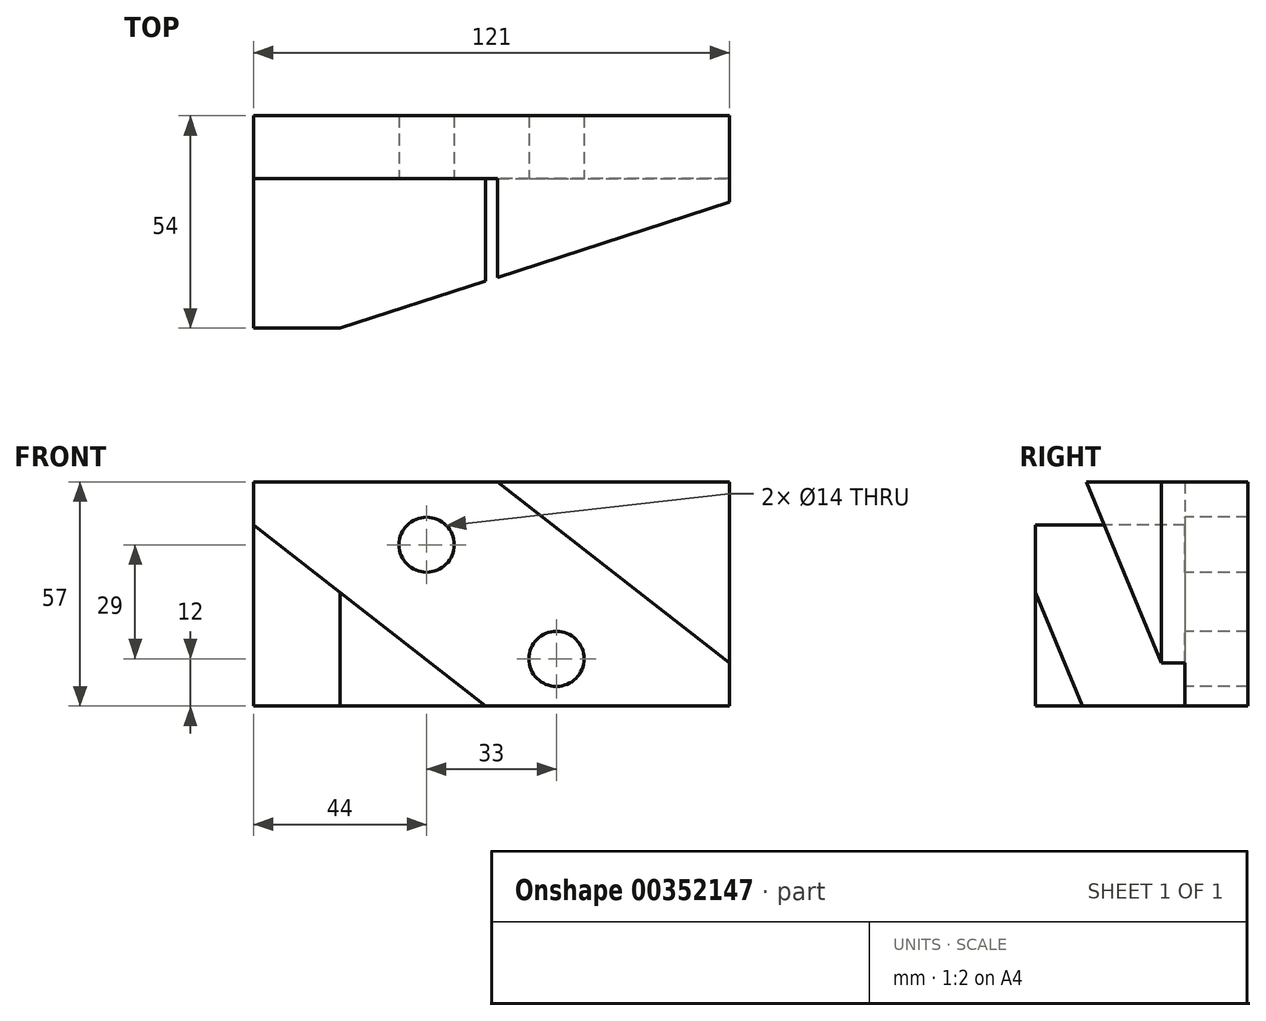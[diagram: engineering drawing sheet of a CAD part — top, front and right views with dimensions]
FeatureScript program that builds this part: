
annotation { "Feature Type Name" : "Feature", "Feature Type Description" : "" }
export const myFeature = defineFeature(function(context is Context, id is Id, definition is map)
    precondition{}
    {
        {
            var Q0;
            Q0=qCreatedBy(makeId("Front.planeOp"),FACE);
            var sketch = newSketch(context, id + "F0", { "sketchPlane" : qUnion([Q0])});
            skLineSegment(sketch, "E0", {"start": v(0, 0) * mm, "end": v(0, 46) * mm});
            skLineSegment(sketch, "E1", {"start": v(22, 28.85) * mm, "end": v(22, 0) * mm});
            skLineSegment(sketch, "E2", {"start": v(0, 46) * mm, "end": v(59, 0) * mm});
            skLineSegment(sketch, "E3", {"start": v(0, 0) * mm, "end": v(59, 0) * mm});
            skLineSegment(sketch, "E4", {"start": v(0, 46) * mm, "end": v(0, 57) * mm});
            skLineSegment(sketch, "E5", {"start": v(0, 57) * mm, "end": v(121, 57) * mm});
            skLineSegment(sketch, "E6", {"start": v(121, 57) * mm, "end": v(121, 0) * mm});
            skLineSegment(sketch, "E7", {"start": v(121, 0) * mm, "end": v(59, 0) * mm});
            skLineSegment(sketch, "E8", {"start": v(62, 57) * mm, "end": v(121, 11) * mm});
            skCircle(sketch, "E9", {"center": v(44, 41) * mm, "radius": 7 * mm});
            skCircle(sketch, "E10", {"center": v(77, 12) * mm, "radius": 7 * mm});
            skPoint(sketch, "E11", {"position": v(59, 57) * mm});
            skSolve(sketch);
        }
        {
            var Q0;
            {var subQ0=sQuery(id+"F0.wireOp",EDGE,"E0");Q0=makeQuery(id+"F0.imprint","IMPRINT",FACE,{"disambiguationData":[TD([[makeQuery(id+"F0.imprint","IMPRINT",EDGE,{"derivedFrom":subQ0}),-1.0]])]});}
            var Q1;
            {var subQ0=sQuery(id+"F0.wireOp",EDGE,"E1");Q1=makeQuery(id+"F0.imprint","IMPRINT",FACE,{"disambiguationData":[TD([[makeQuery(id+"F0.imprint","IMPRINT",EDGE,{"derivedFrom":subQ0}),1.0]])]});}
            var Q2;
            {var subQ3=sQuery(id+"F0.wireOp",EDGE,"E8");Q2=makeQuery(id+"F0.imprint","IMPRINT",FACE,{"disambiguationData":[TD([[makeQuery(id+"F0.imprint","IMPRINT",EDGE,{"derivedFrom":subQ3}),1.0]])]});}
            var Q3;
            {var subQ0=sQuery(id+"F0.wireOp",EDGE,"E4");Q3=makeQuery(id+"F0.imprint","IMPRINT",FACE,{"disambiguationData":[TD([[makeQuery(id+"F0.imprint","IMPRINT",EDGE,{"derivedFrom":subQ0}),-1.0]])]});}
            extrude(context, id + "F1", {"entities" : qUnion([Q0, Q1, Q2, Q3]), "oppositeDirection" : true, "depth" : 38 * mm});
        }
        {
            var Q0;
            Q0=makeQuery(id+"F1.opExtrude","SWEPT_FACE",FACE,{"disambiguationData":[OSD([sQuery(id+"F0.wireOp",EDGE,"E3"),sQuery(id+"F0.wireOp",EDGE,"E7")])]});
            var sketch = newSketch(context, id + "F2", { "sketchPlane" : qUnion([Q0])});
            skLineSegment(sketch, "E12", {"start": v(0, 0) * mm, "end": v(22, 0) * mm});
            skLineSegment(sketch, "E13", {"start": v(22, 0) * mm, "end": v(121, -32) * mm});
            skLineSegment(sketch, "E14", {"start": v(121, 0) * mm, "end": v(121, -32) * mm});
            skSolve(sketch);
        }
        {
            var Q0;
            {var subQ0=sQuery(id+"F2.wireOp",EDGE,"E13");Q0=makeQuery(id+"F2.imprint","IMPRINT",FACE,{"disambiguationData":[TD([[makeQuery(id+"F2.imprint","IMPRINT",EDGE,{"derivedFrom":subQ0}),1.0]])]});}
            extrude(context, id + "F3", {"entities" : qUnion([Q0]), "operationType" : NewBodyOperationType.REMOVE, "oppositeDirection" : true, "depth" : 57 * mm});
        }
        {
            var Q0;
            {var subQ0=sQuery(id+"F0.wireOp",EDGE,"E4");Q0=makeQuery(id+"F0.imprint","IMPRINT",FACE,{"disambiguationData":[TD([[makeQuery(id+"F0.imprint","IMPRINT",EDGE,{"derivedFrom":subQ0}),-1.0]])]});}
            extrude(context, id + "F4", {"entities" : qUnion([Q0]), "operationType" : NewBodyOperationType.REMOVE, "oppositeDirection" : true, "depth" : 54 * mm});
        }
        {
            var Q0;
            Q0=qCreatedBy(makeId("Top.planeOp"),FACE);
            var sketch = newSketch(context, id + "F5", { "sketchPlane" : qUnion([Q0])});
            skLineSegment(sketch, "E15", {"start": v(0, 38) * mm, "end": v(0, 54) * mm});
            skLineSegment(sketch, "E16", {"start": v(0, 54) * mm, "end": v(121, 54) * mm});
            skLineSegment(sketch, "E17", {"start": v(121, 54) * mm, "end": v(121, 38) * mm});
            skLineSegment(sketch, "E18", {"start": v(121, 38) * mm, "end": v(0, 38) * mm});
            skSolve(sketch);
        }
        {
            var Q0;
            Q0=makeQuery(id+"F5.imprint","IMPRINT",FACE,{"disambiguationData":[TD([[makeQuery(id+"F5.imprint","IMPRINT",EDGE,{"derivedFrom":sQuery(id+"F5.wireOp",EDGE,"E15")}),-1.0]])]});
            extrude(context, id + "F6", {"entities" : qUnion([Q0]), "operationType" : NewBodyOperationType.ADD, "depth" : 57 * mm});
        }
        {
            var Q0;
            Q0=makeQuery(id+"F0.imprint","IMPRINT",FACE,{"disambiguationData":[TD([[makeQuery(id+"F0.imprint","IMPRINT",EDGE,{"derivedFrom":sQuery(id+"F0.wireOp",EDGE,"E9")}),1.0]])]});
            var Q1;
            Q1=makeQuery(id+"F0.imprint","IMPRINT",FACE,{"disambiguationData":[TD([[makeQuery(id+"F0.imprint","IMPRINT",EDGE,{"derivedFrom":sQuery(id+"F0.wireOp",EDGE,"E10")}),1.0]])]});
            var Q2;
            Q2=sQuery(id+"F0.wireOp",EDGE,"E9");
            var Q3;
            Q3=sQuery(id+"F0.wireOp",EDGE,"E10");
            extrude(context, id + "F7", {"entities" : qUnion([Q0, Q1]), "operationType" : NewBodyOperationType.REMOVE, "surfaceEntities" : qUnion([Q2, Q3]), "oppositeDirection" : true, "depth" : 54 * mm, "hasSecondDirection" : true, "secondDirectionOppositeDirection" : true, "secondDirectionDepth" : 38 * mm});
        }
    });
